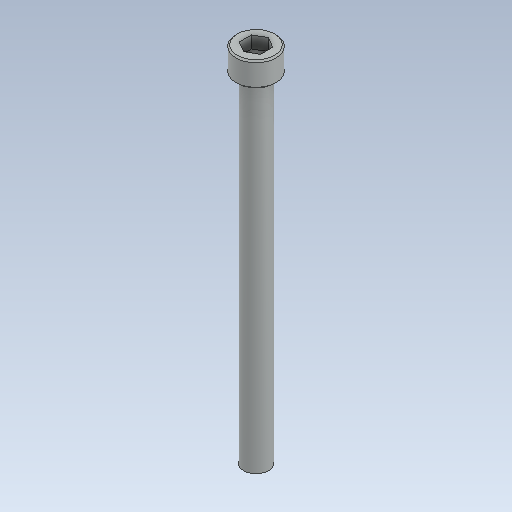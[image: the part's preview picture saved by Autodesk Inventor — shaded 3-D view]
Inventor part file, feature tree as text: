
AUTODESK INVENTOR PART (.ipt)
format: ipt  version: 2020 (Build 240168000, 168)  size: 93,696 bytes
history: native  units: in
note: dims shown in document units (in); Inventor stores cm internally (conversion verified against a paired STEP export)
features: chamfer x1
ambient origin geometry x8: Origin, YZ Plane, XZ Plane, XY Plane, X Axis, Y Axis, Z Axis, Center Point
bodies: Solid1 (feature_tree)
feature tree (1):
  chamfer  "Chamfer2"  [1 undecoded]
note: 1 required parameter value undecoded (feature->parameter linkage not recoverable at this tier; creation-order binding heuristic only, values carry confidence <= 0.55)
